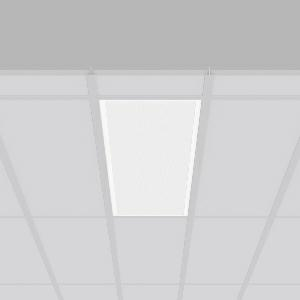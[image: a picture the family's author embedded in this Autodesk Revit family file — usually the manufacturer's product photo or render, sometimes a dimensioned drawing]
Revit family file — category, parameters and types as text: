
# Revit family: sidelite_eco_672367_002_044d
name_source: partatom
category: Lighting Fixtures
units: mm (PartAtom-declared; Revit-internal decimal feet)

## family parameters
Cut with Voids When Loaded = No
Host = Face
Light Source = No
Part Type = Normal
Room Calculation Point = No
Round Connector Dimension = Use Diameter
Shared = No

## types (1)
- SIDELITE ECO (1 x LED Modul 830, 3200 lm, 3000)
    Apparent Load = 29 VA
    CIE Flux Codes = 59 87 97 100 100
    Color Rendering = 80
    Color Temperature = 3000
    Default Elevation = 1800 mm
    Description = Series: SIDELITE ECO
Highly economical recessed luminaire with progressive LED technology. For escape route illumination. Frame made of aluminium, powder-coated. Diffuser plastic microprismatic. Lightguide and diffuser made of non-yellowing plastic (PMMA). Lateral light emission (RZB SIDELITE technology) for homogeneous light distribution. External driver. Second cable inlet for loop through. External driver with simple plug-in locking system. Extended connection cable (1.90 m). Suitable for connection to central battery systems. Luminaire can be used with accessories (to be ordered separately) for recessed, surface mounting or as pendant luminaire. 
Colour: white
Length: 1195 mm
Width: 295 mm
Cut-out length: 1170 mm
Cut-out width: 270 mm
Recess height: 160 mm
Luminaire: recess height: 40 mm
Weight: 3.39 kg
Operating mode: maintained power mode
Lamp: LED
Socket: without socket
Colour temperature: 3000K
Colour rendering index (CRI): 80
System power: 29 W
Rated luminous flux: 3200 lm
Luminous flux, emergency: 3200 lm
System power, emergency: 29 W
Control gear: Regulated power supply
Protection class: II
Type of protection: IP 20
    Height = 0 mm  [stored 0 ft]
    Lamp = 1 x LED Modul 830
    Lamp Light Flux = 3200 lm
    Lamp count = 1
    Length = 1195 mm
    Lifetime = 50000 h
    Luminous efficacy = 110 lm/W
    Manufacturer = RZB
    ModVariant = No
    Model = 672367.002
    Mounting Place = Ceiling
    Mounting Type = Recessed
    Number of Poles = 1
    OnlyDefault = Yes
    Power Factor = 1
    Product Name = SIDELITE ECO
    Product group = Recessed modular luminaires
    ProductGroupID = 406
    Protection Class = Protection class II
    Protection Degree = IP 20
    RLX_Detail_Level = 1
    RLX_Emergency_Light_Flux = 3200 lm
    RLX_Emergency_Type = 3
    RLX_Emergency_Type_DB = Yes
    RlxData = <blob elided: 34793 chars, md5=442ebb2b>
    Socket = socket
    Standby Power = 0 W
    System Light Flux = 3200 lm
    System Power = 29 W
    Type Comments = Product without accessories
    Type Image = 312366.002.jpg
    URL = http://relux.com
    VarID = ---
    Voltage = 230 V
    Voltage Range = 220-240 V
    Weight = 0.00 kg
    Width = 295 mm

note: [stored X ft] marks values corroborated as IEEE doubles in the binary element streams (Revit-internal decimal feet)

## geometry (parser evidence)
native form markers: Blend x4, Sweep x12
no freeform markers — native parametric forms only
